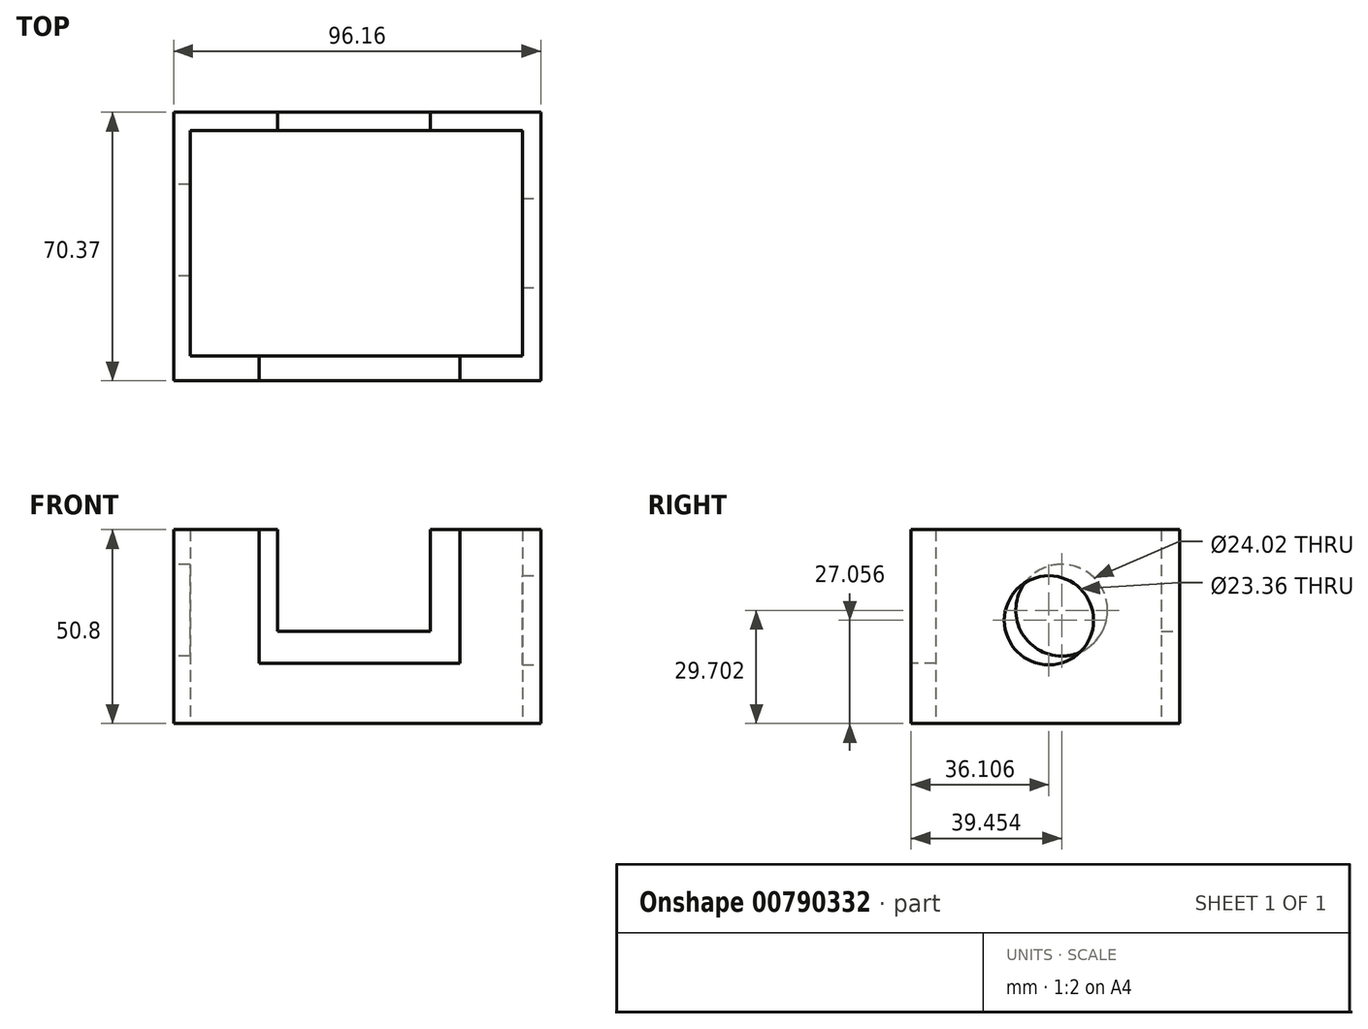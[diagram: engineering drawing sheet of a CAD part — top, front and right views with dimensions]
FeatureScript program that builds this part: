
annotation { "Feature Type Name" : "Feature", "Feature Type Description" : "" }
export const myFeature = defineFeature(function(context is Context, id is Id, definition is map)
    precondition{}
    {
        {
            var Q0;
            Q0=qCreatedBy(makeId("Top.planeOp"),FACE);
            var sketch = newSketch(context, id + "F0", { "sketchPlane" : qUnion([Q0])});
            skLineSegment(sketch, "E0.bottom", {"start": v(-40.37, 37.72) * mm, "end": v(55.8, 37.72) * mm});
            skLineSegment(sketch, "E0.top", {"start": v(-36.03, 32.9) * mm, "end": v(50.97, 32.9) * mm});
            skLineSegment(sketch, "E0.left", {"start": v(-40.37, 37.72) * mm, "end": v(-40.37, 32.9) * mm});
            skLineSegment(sketch, "E0.right", {"start": v(55.8, 37.72) * mm, "end": v(55.8, 32.9) * mm});
            skLineSegment(sketch, "E1.top", {"start": v(55.8, -32.65) * mm, "end": v(50.97, -32.65) * mm});
            skLineSegment(sketch, "E1.left", {"start": v(55.8, 32.9) * mm, "end": v(55.8, -32.65) * mm});
            skLineSegment(sketch, "E1.right", {"start": v(50.97, 32.9) * mm, "end": v(50.97, -26.15) * mm});
            skLineSegment(sketch, "E2.bottom", {"start": v(50.97, -32.65) * mm, "end": v(-40.37, -32.65) * mm});
            skLineSegment(sketch, "E2.top", {"start": v(50.97, -26.15) * mm, "end": v(-36.03, -26.15) * mm});
            skLineSegment(sketch, "E2.right", {"start": v(-40.37, -32.65) * mm, "end": v(-40.37, -26.15) * mm});
            skLineSegment(sketch, "E3.bottom", {"start": v(-40.37, -26.15) * mm, "end": v(-40.37, -26.15) * mm});
            skLineSegment(sketch, "E3.top", {"start": v(-40.37, 32.9) * mm, "end": v(-40.37, 32.9) * mm});
            skLineSegment(sketch, "E3.left", {"start": v(-40.37, -26.15) * mm, "end": v(-40.37, 32.9) * mm});
            skLineSegment(sketch, "E3.right", {"start": v(-40.37, -26.15) * mm, "end": v(-40.37, 32.9) * mm});
            skLineSegment(sketch, "E4.left", {"start": v(-40.37, 32.9) * mm, "end": v(-40.37, -26.15) * mm});
            skLineSegment(sketch, "E4.right", {"start": v(-36.03, 32.9) * mm, "end": v(-36.03, -26.15) * mm});
            skSolve(sketch);
        }
        {
            var Q0;
            Q0=makeQuery(id+"F0.imprint","IMPRINT",FACE,{"disambiguationData":[TD([[makeQuery(id+"F0.imprint","IMPRINT",EDGE,{"derivedFrom":sQuery(id+"F0.wireOp",EDGE,"E0.bottom")}),-1.0]])]});
            extrude(context, id + "F1", {"entities" : qUnion([Q0]), "depth" : 50.8 * mm, "offsetDistance" : 25.4 * mm});
        }
        {
            var Q0;
            Q0=makeQuery(id+"F1.opExtrude","SWEPT_FACE",FACE,{"disambiguationData":[OSD([sQuery(id+"F0.wireOp",EDGE,"E0.left"),sQuery(id+"F0.wireOp",EDGE,"E2.right"),sQuery(id+"F0.wireOp",EDGE,"E4.left")])]});
            var sketch = newSketch(context, id + "F2", { "sketchPlane" : qUnion([Q0])});
            skCircle(sketch, "E5", {"center": v(-6.8, 29.7) * mm, "radius": 12.01 * mm});
            skSolve(sketch);
        }
        {
            var Q0;
            Q0=makeQuery(id+"F1.opExtrude","SWEPT_FACE",FACE,{"disambiguationData":[OSD([sQuery(id+"F0.wireOp",EDGE,"E1.top"),sQuery(id+"F0.wireOp",EDGE,"E2.bottom")])]});
            var sketch = newSketch(context, id + "F3", { "sketchPlane" : qUnion([Q0])});
            skLineSegment(sketch, "E6.bottom", {"start": v(-18, 50.8) * mm, "end": v(34.59, 50.8) * mm});
            skLineSegment(sketch, "E6.top", {"start": v(-18, 15.75) * mm, "end": v(34.59, 15.75) * mm});
            skLineSegment(sketch, "E6.left", {"start": v(-18, 50.8) * mm, "end": v(-18, 15.75) * mm});
            skLineSegment(sketch, "E6.right", {"start": v(34.59, 50.8) * mm, "end": v(34.59, 15.75) * mm});
            skSolve(sketch);
        }
        {
            var Q0;
            Q0 = qSketchRegion(id + "F3", true);
            extrude(context, id + "F4", {"entities" : qUnion([Q0]), "operationType" : NewBodyOperationType.REMOVE, "oppositeDirection" : true, "depth" : 25.4 * mm, "offsetDistance" : 25.4 * mm});
        }
        {
            var Q0;
            Q0=makeQuery(id+"F1.opExtrude","SWEPT_FACE",FACE,{"disambiguationData":[OSD([sQuery(id+"F0.wireOp",EDGE,"E0.bottom")])]});
            var sketch = newSketch(context, id + "F5", { "sketchPlane" : qUnion([Q0])});
            skLineSegment(sketch, "E7.bottom", {"start": v(-26.87, 50.8) * mm, "end": v(13.13, 50.8) * mm});
            skLineSegment(sketch, "E7.top", {"start": v(-26.87, 24.22) * mm, "end": v(13.13, 24.22) * mm});
            skLineSegment(sketch, "E7.left", {"start": v(-26.87, 50.8) * mm, "end": v(-26.87, 24.22) * mm});
            skLineSegment(sketch, "E7.right", {"start": v(13.13, 50.8) * mm, "end": v(13.13, 24.22) * mm});
            skSolve(sketch);
        }
        {
            var Q0;
            Q0=makeQuery(id+"F5.imprint","IMPRINT",FACE,{"disambiguationData":[TD([[makeQuery(id+"F5.imprint","IMPRINT",EDGE,{"derivedFrom":sQuery(id+"F5.wireOp",EDGE,"E7.bottom")}),1.0]])]});
            extrude(context, id + "F6", {"entities" : qUnion([Q0]), "operationType" : NewBodyOperationType.REMOVE, "oppositeDirection" : true, "depth" : 25.4 * mm, "offsetDistance" : 25.4 * mm});
        }
        {
            var Q0;
            Q0 = qSketchRegion(id + "F2", true);
            extrude(context, id + "F7", {"entities" : qUnion([Q0]), "operationType" : NewBodyOperationType.REMOVE, "oppositeDirection" : true, "depth" : 25.4 * mm, "offsetDistance" : 25.4 * mm});
        }
        {
            var Q0;
            Q0=makeQuery(id+"F1.opExtrude","SWEPT_FACE",FACE,{"disambiguationData":[OSD([sQuery(id+"F0.wireOp",EDGE,"E0.right"),sQuery(id+"F0.wireOp",EDGE,"E1.left")])]});
            var sketch = newSketch(context, id + "F8", { "sketchPlane" : qUnion([Q0])});
            skCircle(sketch, "E8", {"center": v(3.46, 27.06) * mm, "radius": 11.68 * mm});
            skSolve(sketch);
        }
        {
            var Q0;
            Q0=makeQuery(id+"F8.imprint","IMPRINT",FACE,{"disambiguationData":[TD([[makeQuery(id+"F8.imprint","IMPRINT",EDGE,{"derivedFrom":sQuery(id+"F8.wireOp",EDGE,"E8")}),1.0]])]});
            extrude(context, id + "F9", {"entities" : qUnion([Q0]), "operationType" : NewBodyOperationType.REMOVE, "oppositeDirection" : true, "depth" : 25.4 * mm, "offsetDistance" : 25.4 * mm});
        }
    });
